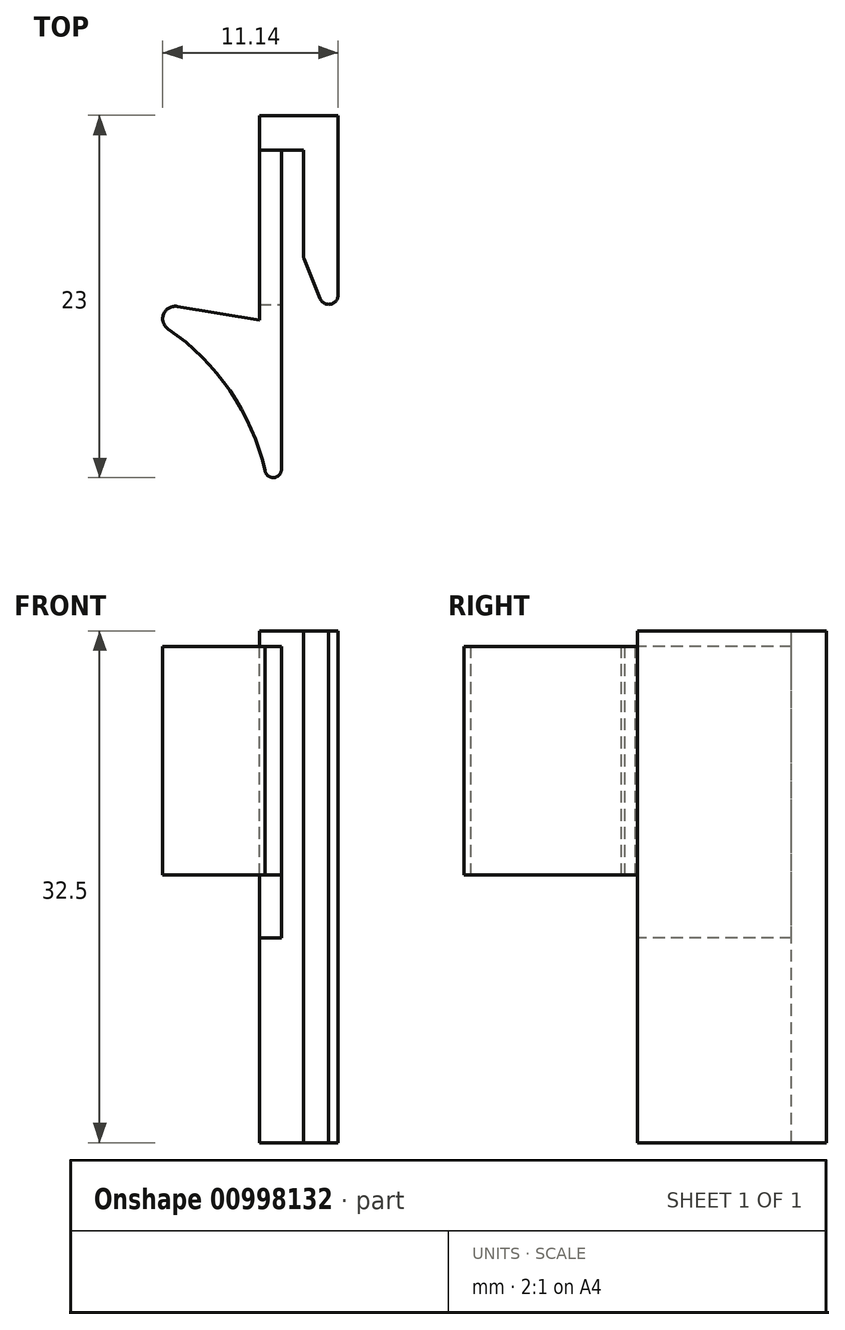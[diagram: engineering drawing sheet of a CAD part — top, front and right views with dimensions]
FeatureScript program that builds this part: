
annotation { "Feature Type Name" : "Feature", "Feature Type Description" : "" }
export const myFeature = defineFeature(function(context is Context, id is Id, definition is map)
    precondition{}
    {
        {
            var Q0;
            Q0=qCreatedBy(makeId("Top.planeOp"),FACE);
            var sketch = newSketch(context, id + "F0", { "sketchPlane" : qUnion([Q0])});
            skLineSegment(sketch, "E0", {"start": v(-37.07, 18.3) * mm, "end": v(-32.07, 18.3) * mm});
            skLineSegment(sketch, "E1", {"start": v(-32.07, 18.3) * mm, "end": v(-32.07, 6.9) * mm});
            skLineSegment(sketch, "E2", {"start": v(-32.67, 6.3) * mm, "end": v(-32.67, 6.3) * mm});
            skLineSegment(sketch, "E3", {"start": v(-34.27, 9.41) * mm, "end": v(-34.27, 16.1) * mm});
            skLineSegment(sketch, "E4", {"start": v(-33.22, 6.67) * mm, "end": v(-34.23, 9.2) * mm});
            skLineSegment(sketch, "E5", {"start": v(-34.27, 16.1) * mm, "end": v(-35.67, 16.1) * mm});
            skLineSegment(sketch, "E6", {"start": v(-35.67, 16.1) * mm, "end": v(-35.67, -4.2) * mm});
            skLineSegment(sketch, "E7", {"start": v(-37.07, 18.3) * mm, "end": v(-37.07, 5.3) * mm});
            skLineSegment(sketch, "E8", {"start": v(-37.07, 6.3) * mm, "end": v(-43.07, 6.3) * mm, "construction": true});
            skLineSegment(sketch, "E9", {"start": v(-36.21, -4.7) * mm, "end": v(-36.17, -4.7) * mm});
            skPoint(sketch, "E10.visualSharp", {"position": v(-43.07, 6.3) * mm});
            skPoint(sketch, "E11.visualSharp", {"position": v(-37.07, -4.7) * mm});
            skArc(sketch, "E11.filletArc", {"start": v(-36.7, -4.27) * mm, "mid": v(-36.54, -4.58) * mm, "end": v(-36.21, -4.7) * mm});
            skPoint(sketch, "E12.visualSharp", {"position": v(-35.67, -4.7) * mm});
            skArc(sketch, "E12.filletArc", {"start": v(-36.17, -4.7) * mm, "mid": v(-35.82, -4.56) * mm, "end": v(-35.67, -4.2) * mm});
            skPoint(sketch, "E13.visualSharp", {"position": v(-33.07, 6.3) * mm});
            skArc(sketch, "E13.filletArc", {"start": v(-33.22, 6.67) * mm, "mid": v(-33, 6.4) * mm, "end": v(-32.67, 6.3) * mm});
            skPoint(sketch, "E14.visualSharp", {"position": v(-32.07, 6.3) * mm});
            skArc(sketch, "E14.filletArc", {"start": v(-32.67, 6.3) * mm, "mid": v(-32.25, 6.47) * mm, "end": v(-32.07, 6.9) * mm});
            skPoint(sketch, "E15.visualSharp", {"position": v(-34.27, 9.3) * mm});
            skArc(sketch, "E15.filletArc", {"start": v(-34.27, 9.41) * mm, "mid": v(-34.26, 9.3) * mm, "end": v(-34.23, 9.2) * mm});
            skLineSegment(sketch, "E16", {"start": v(-37.07, 5.3) * mm, "end": v(-42.28, 6.17) * mm});
            skLineSegment(sketch, "E17", {"start": v(-43.2, 5.53) * mm, "end": v(-43.2, 5.5) * mm});
            skArc(sketch, "E18", {"start": v(-36.7, -4.27) * mm, "mid": v(-38.94, 0.8) * mm, "end": v(-42.87, 4.74) * mm});
            skPoint(sketch, "E19.visualSharp", {"position": v(-43.29, 5.02) * mm});
            skArc(sketch, "E19.filletArc", {"start": v(-43.2, 5.53) * mm, "mid": v(-43.15, 5.08) * mm, "end": v(-42.87, 4.74) * mm});
            skArc(sketch, "E20.filletArc", {"start": v(-42.28, 6.17) * mm, "mid": v(-42.88, 6.03) * mm, "end": v(-43.2, 5.5) * mm});
            skLineSegment(sketch, "E21", {"start": v(-35.67, 16.1) * mm, "end": v(-37.07, 16.1) * mm});
            skLineSegment(sketch, "E22", {"start": v(-37.07, 6.3) * mm, "end": v(-35.67, 6.3) * mm});
            skSolve(sketch);
        }
        {
            var Q0;
            Q0=makeQuery(id+"F0.imprint","IMPRINT",FACE,{"disambiguationData":[TD([[makeQuery(id+"F0.imprint","IMPRINT",EDGE,{"derivedFrom":sQuery(id+"F0.wireOp",EDGE,"E0")}),-1.0]])]});
            var Q1;
            {var subQ0=sQuery(id+"F0.wireOp",EDGE,"E21");Q1=makeQuery(id+"F0.imprint","IMPRINT",FACE,{"disambiguationData":[TD([[makeQuery(id+"F0.imprint","IMPRINT",EDGE,{"derivedFrom":subQ0}),1.0]])]});}
            var Q2;
            Q2=makeQuery(id+"F0.imprint","IMPRINT",FACE,{"disambiguationData":[TD([[makeQuery(id+"F0.imprint","IMPRINT",EDGE,{"derivedFrom":sQuery(id+"F0.wireOp",EDGE,"E9")}),1.0]])]});
            extrude(context, id + "F1", {"entities" : qUnion([Q0, Q1, Q2]), "oppositeDirection" : true, "depth" : 15.5 * mm, "offsetDistance" : 25 * mm});
        }
        {
            var Q0;
            {var subQ0=sQuery(id+"F0.wireOp",EDGE,"E21");Q0=makeQuery(id+"F0.imprint","IMPRINT",FACE,{"disambiguationData":[TD([[makeQuery(id+"F0.imprint","IMPRINT",EDGE,{"derivedFrom":subQ0}),1.0]])]});}
            extrude(context, id + "F2", {"entities" : qUnion([Q0]), "operationType" : NewBodyOperationType.ADD, "oppositeDirection" : true, "depth" : 19.5 * mm, "offsetDistance" : 25 * mm});
        }
        {
            var Q0;
            {var subQ0=sQuery(id+"F0.wireOp",EDGE,"E21");Q0=makeQuery(id+"F0.imprint","IMPRINT",FACE,{"disambiguationData":[TD([[makeQuery(id+"F0.imprint","IMPRINT",EDGE,{"derivedFrom":subQ0}),1.0]])]});}
            var Q1;
            Q1=makeQuery(id+"F0.imprint","IMPRINT",FACE,{"disambiguationData":[TD([[makeQuery(id+"F0.imprint","IMPRINT",EDGE,{"derivedFrom":sQuery(id+"F0.wireOp",EDGE,"E9")}),1.0]])]});
            extrude(context, id + "F3", {"entities" : qUnion([Q0, Q1]), "operationType" : NewBodyOperationType.REMOVE, "oppositeDirection" : true, "depth" : 1 * mm, "offsetDistance" : 25 * mm});
        }
        {
            var Q0;
            {var subQ1=sQuery(id+"F0.wireOp",EDGE,"E0");Q0=makeQuery(id+"F0.imprint","IMPRINT",FACE,{"disambiguationData":[TD([[makeQuery(id+"F0.imprint","IMPRINT",EDGE,{"derivedFrom":subQ1}),-1.0]])]});}
            extrude(context, id + "F4", {"entities" : qUnion([Q0]), "operationType" : NewBodyOperationType.ADD, "oppositeDirection" : true, "depth" : 32.5 * mm, "offsetDistance" : 25 * mm});
        }
    });
